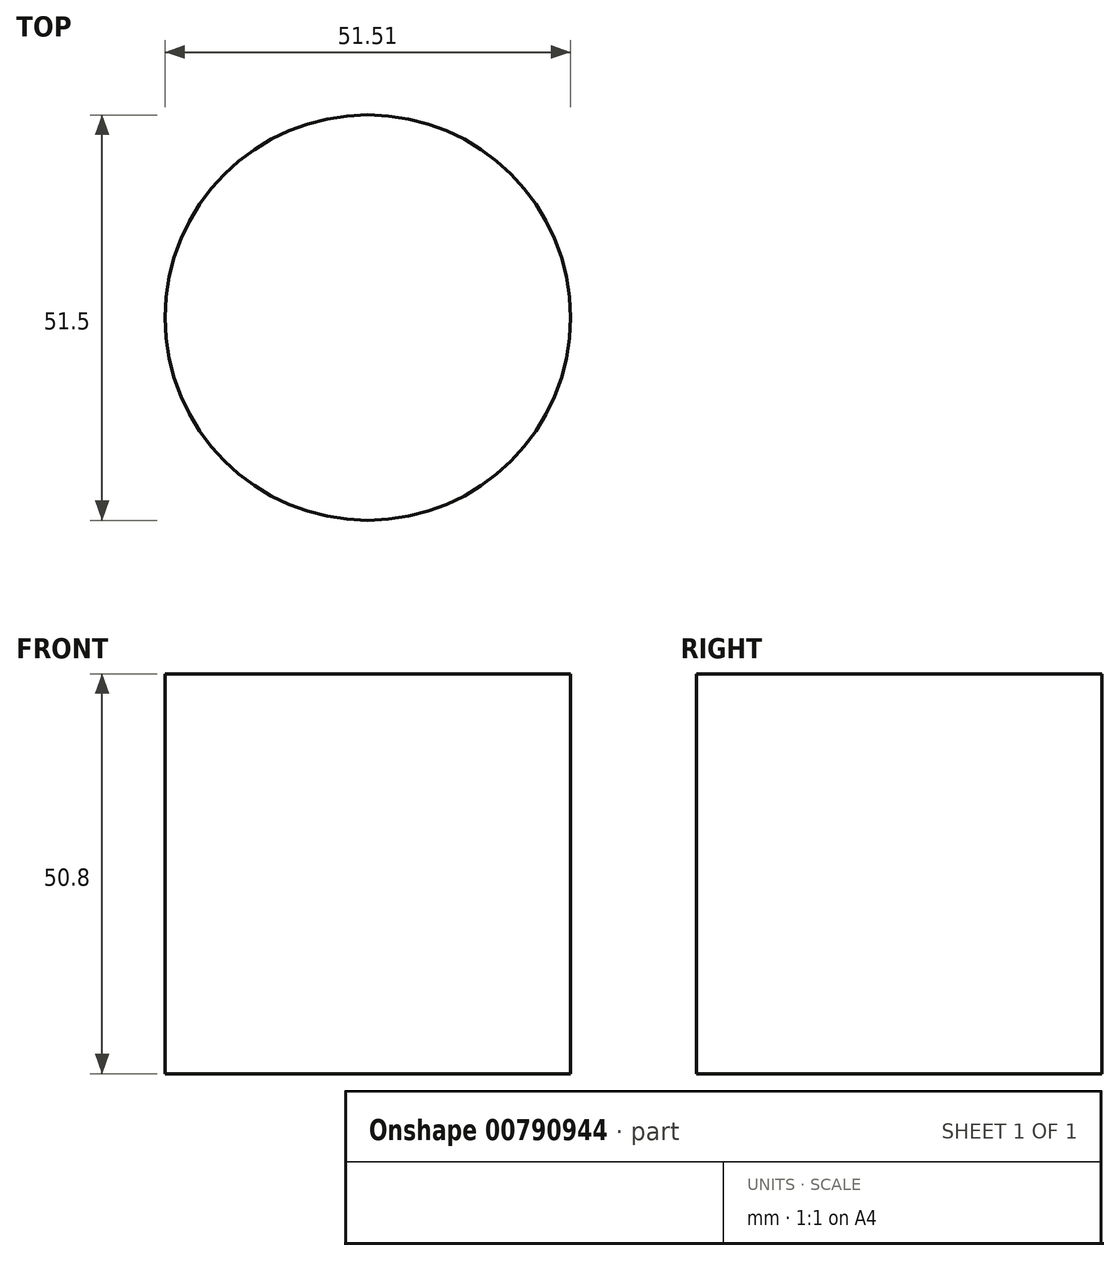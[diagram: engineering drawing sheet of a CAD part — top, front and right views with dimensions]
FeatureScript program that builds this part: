
annotation { "Feature Type Name" : "Feature", "Feature Type Description" : "" }
export const myFeature = defineFeature(function(context is Context, id is Id, definition is map)
    precondition{}
    {
        {
            var Q0;
            Q0=qCreatedBy(makeId("Top.planeOp"),FACE);
            var sketch = newSketch(context, id + "F0", { "sketchPlane" : qUnion([Q0])});
            skCircle(sketch, "E0", {"center": v(23.12, 25.83) * mm, "radius": 25.75 * mm});
            skSolve(sketch);
        }
        {
            var Q0;
            Q0=makeQuery(id+"F0.imprint","IMPRINT",FACE,{"disambiguationData":[TD([[makeQuery(id+"F0.imprint","IMPRINT",EDGE,{"derivedFrom":sQuery(id+"F0.wireOp",EDGE,"E0")}),1.0]])]});
            extrude(context, id + "F1", {"entities" : qUnion([Q0]), "depth" : -50.8 * mm, "offsetDistance" : 25.4 * mm});
        }
    });
